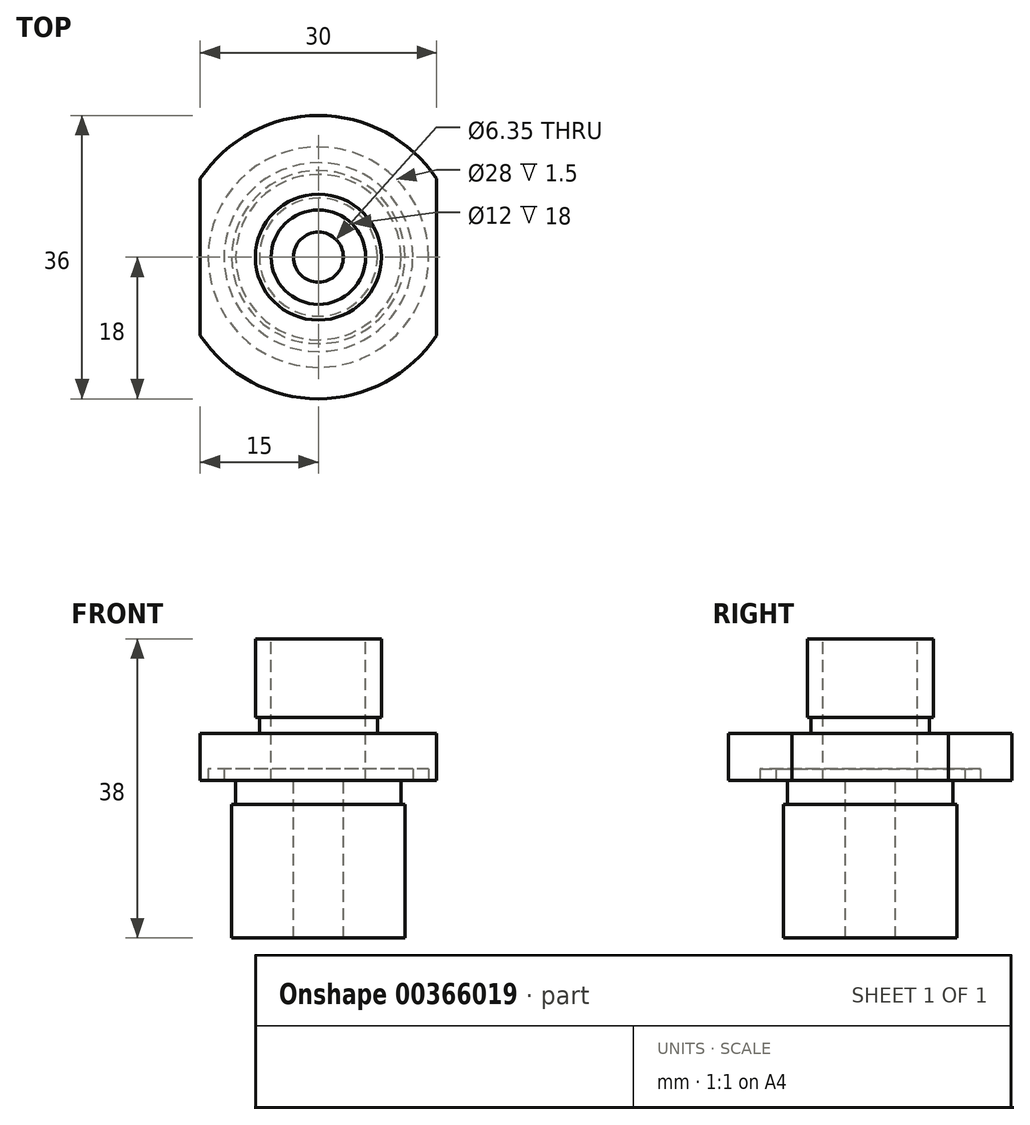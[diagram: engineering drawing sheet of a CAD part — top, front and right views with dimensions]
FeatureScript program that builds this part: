
annotation { "Feature Type Name" : "Feature", "Feature Type Description" : "" }
export const myFeature = defineFeature(function(context is Context, id is Id, definition is map)
    precondition{}
    {
        {
            var Q0;
            Q0=qCreatedBy(makeId("Top.planeOp"),FACE);
            var sketch = newSketch(context, id + "F0", { "sketchPlane" : qUnion([Q0])});
            skArc(sketch, "E0", {"start": v(15, 9.95) * mm, "mid": v(0, 18) * mm, "end": v(-15, 9.95) * mm});
            skLineSegment(sketch, "E1", {"start": v(15, 9.95) * mm, "end": v(15, -9.95) * mm});
            skLineSegment(sketch, "E2", {"start": v(-15, 9.95) * mm, "end": v(-15, -9.95) * mm});
            skArc(sketch, "E3.trimOffspring", {"start": v(-15, -9.95) * mm, "mid": v(0, -18) * mm, "end": v(15, -9.95) * mm});
            skSolve(sketch);
        }
        {
            var Q0;
            Q0=makeQuery(id+"F0.imprint","IMPRINT",FACE,{"disambiguationData":[TD([[makeQuery(id+"F0.imprint","IMPRINT",EDGE,{"derivedFrom":sQuery(id+"F0.wireOp",EDGE,"E0")}),1.0]])]});
            extrude(context, id + "F1", {"entities" : qUnion([Q0]), "depth" : 6 * mm});
        }
        {
            var Q0;
            Q0=qCreatedBy(makeId("Top.planeOp"),FACE);
            var sketch = newSketch(context, id + "F2", { "sketchPlane" : qUnion([Q0])});
            skCircle(sketch, "E4", {"center": v(0, 0) * mm, "radius": 12 * mm});
            skCircle(sketch, "E5", {"center": v(0, 0) * mm, "radius": 14 * mm});
            skSolve(sketch);
        }
        {
            var Q0;
            Q0=makeQuery(id+"F2.imprint","IMPRINT",FACE,{"disambiguationData":[TD([[makeQuery(id+"F2.imprint","IMPRINT",EDGE,{"derivedFrom":sQuery(id+"F2.wireOp",EDGE,"E4")}),-1.0]])]});
            extrude(context, id + "F3", {"entities" : qUnion([Q0]), "operationType" : NewBodyOperationType.REMOVE, "depth" : 1.5 * mm});
        }
        {
            var Q0;
            Q0=qCreatedBy(makeId("Top.planeOp"),FACE);
            var sketch = newSketch(context, id + "F4", { "sketchPlane" : qUnion([Q0])});
            skCircle(sketch, "E6", {"center": v(0, 0) * mm, "radius": 10.5 * mm});
            skSolve(sketch);
        }
        {
            var Q0;
            Q0=makeQuery(id+"F4.imprint","IMPRINT",FACE,{"disambiguationData":[TD([[makeQuery(id+"F4.imprint","IMPRINT",EDGE,{"derivedFrom":sQuery(id+"F4.wireOp",EDGE,"E6")}),1.0]])]});
            extrude(context, id + "F5", {"entities" : qUnion([Q0]), "operationType" : NewBodyOperationType.ADD, "oppositeDirection" : true, "depth" : 3 * mm});
        }
        {
            var Q0;
            Q0=makeQuery(id+"F5.opExtrude","CAP_FACE",FACE,{"disambiguationData":[OSD([sQuery(id+"F4.wireOp",EDGE,"E6")])],"isStart":false});
            cPlane(context, id + "F6", {"entities" : qUnion([Q0]), "cplaneType" : CPlaneType.OFFSET, "offset" : 0 * mm, "width" : 150 * mm, "height" : 150 * mm});
        }
        {
            var Q0;
            Q0=qCreatedBy(id+"F6.planeOp",FACE);
            var sketch = newSketch(context, id + "F7", { "sketchPlane" : qUnion([Q0])});
            skCircle(sketch, "E7", {"center": v(0, 0) * mm, "radius": 11 * mm});
            skSolve(sketch);
        }
        {
            var Q0;
            Q0=makeQuery(id+"F7.imprint","IMPRINT",FACE,{"disambiguationData":[TD([[makeQuery(id+"F7.imprint","IMPRINT",EDGE,{"derivedFrom":sQuery(id+"F7.wireOp",EDGE,"E7")}),1.0]])]});
            extrude(context, id + "F8", {"entities" : qUnion([Q0]), "operationType" : NewBodyOperationType.ADD, "depth" : 17 * mm});
        }
        {
            var Q0;
            Q0=makeQuery(id+"F1.opExtrude","CAP_FACE",FACE,{"disambiguationData":[OSD([sQuery(id+"F0.wireOp",EDGE,"E0"),sQuery(id+"F0.wireOp",EDGE,"E1"),sQuery(id+"F0.wireOp",EDGE,"E2"),sQuery(id+"F0.wireOp",EDGE,"E3.trimOffspring")])],"isStart":false});
            cPlane(context, id + "F9", {"entities" : qUnion([Q0]), "cplaneType" : CPlaneType.OFFSET, "offset" : 0 * mm, "width" : 150 * mm, "height" : 150 * mm});
        }
        {
            var Q0;
            Q0=qCreatedBy(id+"F9.planeOp",FACE);
            var sketch = newSketch(context, id + "F10", { "sketchPlane" : qUnion([Q0])});
            skCircle(sketch, "E8", {"center": v(0, 0) * mm, "radius": 7.5 * mm});
            skSolve(sketch);
        }
        {
            var Q0;
            Q0=makeQuery(id+"F10.imprint","IMPRINT",FACE,{"disambiguationData":[TD([[makeQuery(id+"F10.imprint","IMPRINT",EDGE,{"derivedFrom":sQuery(id+"F10.wireOp",EDGE,"E8")}),1.0]])]});
            extrude(context, id + "F11", {"entities" : qUnion([Q0]), "operationType" : NewBodyOperationType.ADD, "depth" : 2 * mm});
        }
        {
            var Q0;
            Q0=makeQuery(id+"F11.opExtrude","CAP_FACE",FACE,{"disambiguationData":[OSD([sQuery(id+"F10.wireOp",EDGE,"E8")])],"isStart":false});
            cPlane(context, id + "F12", {"entities" : qUnion([Q0]), "cplaneType" : CPlaneType.OFFSET, "offset" : 0 * mm, "width" : 150 * mm, "height" : 150 * mm});
        }
        {
            var Q0;
            Q0=qCreatedBy(id+"F12.planeOp",FACE);
            var sketch = newSketch(context, id + "F13", { "sketchPlane" : qUnion([Q0])});
            skCircle(sketch, "E9", {"center": v(0, 0) * mm, "radius": 8 * mm});
            skSolve(sketch);
        }
        {
            var Q0;
            Q0=makeQuery(id+"F13.imprint","IMPRINT",FACE,{"disambiguationData":[TD([[makeQuery(id+"F13.imprint","IMPRINT",EDGE,{"derivedFrom":sQuery(id+"F13.wireOp",EDGE,"E9")}),1.0]])]});
            extrude(context, id + "F14", {"entities" : qUnion([Q0]), "operationType" : NewBodyOperationType.ADD, "depth" : 10 * mm});
        }
        {
            var Q0;
            Q0=makeQuery(id+"F14.opExtrude","CAP_FACE",FACE,{"disambiguationData":[OSD([sQuery(id+"F13.wireOp",EDGE,"E9")])],"isStart":false});
            cPlane(context, id + "F15", {"entities" : qUnion([Q0]), "cplaneType" : CPlaneType.OFFSET, "offset" : 0 * mm, "width" : 150 * mm, "height" : 150 * mm});
        }
        {
            var Q0;
            Q0=qCreatedBy(id+"F15.planeOp",FACE);
            var sketch = newSketch(context, id + "F16", { "sketchPlane" : qUnion([Q0])});
            skPoint(sketch, "E10", {"position": v(0, 0) * mm});
            skSolve(sketch);
        }
        {
            var Q0;
            Q0=sQuery(id+"F16.wireOp",VERTEX,"E10");
            var Q1;
            Q1=makeQuery(id+"F1.opExtrude","SWEPT_BODY",BODY,{"disambiguationData":[OSD([sQuery(id+"F0.wireOp",EDGE,"E0"),sQuery(id+"F0.wireOp",EDGE,"E1"),sQuery(id+"F0.wireOp",EDGE,"E2"),sQuery(id+"F0.wireOp",EDGE,"E3.trimOffspring")])]});
            hole(context, id + "F17", {"style" : HoleStyle.SIMPLE, "endStyle" : HoleEndStyle.THROUGH, "holeDiameter" : 6.35 * mm, "isTappedThrough" : true, "tappedDepth" : 2 * mm, "tapClearance" : 3, "startFromSketch" : true, "locations" : qUnion([Q0]), "scope" : qUnion([Q1])});
        }
        {
            var Q0;
            Q0=qCreatedBy(id+"F15.planeOp",FACE);
            var sketch = newSketch(context, id + "F18", { "sketchPlane" : qUnion([Q0])});
            skCircle(sketch, "E11", {"center": v(0, 0) * mm, "radius": 6 * mm});
            skSolve(sketch);
        }
        {
            var Q0;
            Q0=makeQuery(id+"F18.imprint","IMPRINT",FACE,{"disambiguationData":[TD([[makeQuery(id+"F18.imprint","IMPRINT",EDGE,{"derivedFrom":sQuery(id+"F18.wireOp",EDGE,"E11")}),1.0]])]});
            extrude(context, id + "F19", {"entities" : qUnion([Q0]), "operationType" : NewBodyOperationType.REMOVE, "oppositeDirection" : true, "depth" : 18 * mm});
        }
    });
